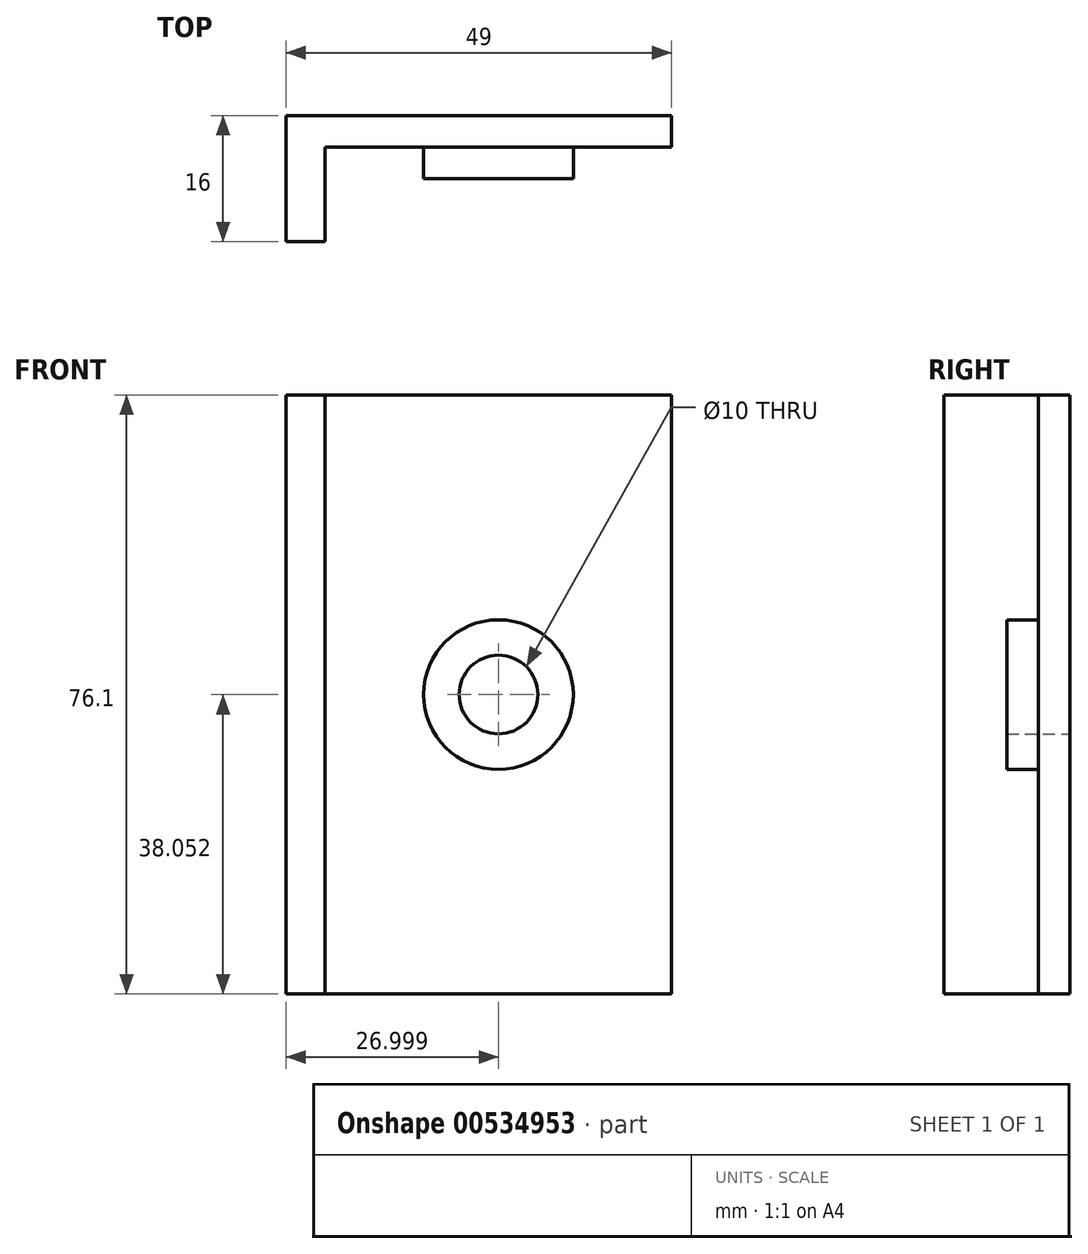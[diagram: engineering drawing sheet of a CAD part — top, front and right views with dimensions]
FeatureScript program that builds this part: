
annotation { "Feature Type Name" : "Feature", "Feature Type Description" : "" }
export const myFeature = defineFeature(function(context is Context, id is Id, definition is map)
    precondition{}
    {
        {
            var Q0;
            Q0=qCreatedBy(makeId("Front.planeOp"),FACE);
            var sketch = newSketch(context, id + "F0", { "sketchPlane" : qUnion([Q0])});
            skLineSegment(sketch, "E0.bottom", {"start": v(-81.87, 32.58) * mm, "end": v(-37.87, 32.58) * mm});
            skLineSegment(sketch, "E0.top", {"start": v(-81.87, -43.52) * mm, "end": v(-37.87, -43.52) * mm});
            skLineSegment(sketch, "E0.left", {"start": v(-81.87, 32.58) * mm, "end": v(-81.87, -43.52) * mm});
            skLineSegment(sketch, "E0.right", {"start": v(-37.87, 32.58) * mm, "end": v(-37.87, -43.52) * mm});
            skLineSegment(sketch, "E1", {"start": v(-81.87, -5.47) * mm, "end": v(-59.87, -5.47) * mm});
            skCircle(sketch, "E2", {"center": v(-59.87, -5.47) * mm, "radius": 5 * mm});
            skSolve(sketch);
        }
        {
            var Q0;
            Q0 = qSketchRegion(id + "F0", true);
            extrude(context, id + "F1", {"entities" : qUnion([Q0]), "depth" : 8 * mm, "offsetDistance" : 25.4 * mm});
        }
        {
            var Q0;
            Q0=makeQuery(id+"F1.opExtrude","SWEPT_FACE",FACE,{"disambiguationData":[OSD([sQuery(id+"F0.wireOp",EDGE,"E0.left")])]});
            var sketch = newSketch(context, id + "F2", { "sketchPlane" : qUnion([Q0])});
            skLineSegment(sketch, "E3.bottom", {"start": v(0, 32.58) * mm, "end": v(16, 32.58) * mm});
            skLineSegment(sketch, "E3.top", {"start": v(0, -43.52) * mm, "end": v(16, -43.52) * mm});
            skLineSegment(sketch, "E3.left", {"start": v(0, 32.58) * mm, "end": v(0, -43.52) * mm});
            skLineSegment(sketch, "E3.right", {"start": v(16, 32.58) * mm, "end": v(16, -43.52) * mm});
            skSolve(sketch);
        }
        {
            var Q0;
            Q0 = qSketchRegion(id + "F2", true);
            extrude(context, id + "F3", {"entities" : qUnion([Q0]), "operationType" : NewBodyOperationType.ADD, "depth" : 5 * mm, "offsetDistance" : 25.4 * mm});
        }
        {
            var Q0;
            Q0=makeQuery(id+"F1.opExtrude","CAP_FACE",FACE,{"disambiguationData":[OSD([sQuery(id+"F0.wireOp",EDGE,"E0.bottom"),sQuery(id+"F0.wireOp",EDGE,"E0.top"),sQuery(id+"F0.wireOp",EDGE,"E0.left"),sQuery(id+"F0.wireOp",EDGE,"E0.right"),sQuery(id+"F0.wireOp",EDGE,"E2")])],"isStart":false});
            var sketch = newSketch(context, id + "F4", { "sketchPlane" : qUnion([Q0])});
            skLineSegment(sketch, "E4.bottom", {"start": v(-81.87, -43.52) * mm, "end": v(-37.87, -43.52) * mm});
            skLineSegment(sketch, "E4.top", {"start": v(-81.87, 32.58) * mm, "end": v(-37.87, 32.58) * mm});
            skLineSegment(sketch, "E4.left", {"start": v(-81.87, -43.52) * mm, "end": v(-81.87, 32.58) * mm});
            skLineSegment(sketch, "E4.right", {"start": v(-37.87, -43.52) * mm, "end": v(-37.87, 32.58) * mm});
            skCircle(sketch, "E5", {"center": v(-59.87, -5.47) * mm, "radius": 9.5 * mm});
            skSolve(sketch);
        }
        {
            var Q0;
            Q0 = qSketchRegion(id + "F4", true);
            extrude(context, id + "F5", {"entities" : qUnion([Q0]), "operationType" : NewBodyOperationType.REMOVE, "oppositeDirection" : true, "depth" : 4 * mm, "offsetDistance" : 25.4 * mm});
        }
    });
